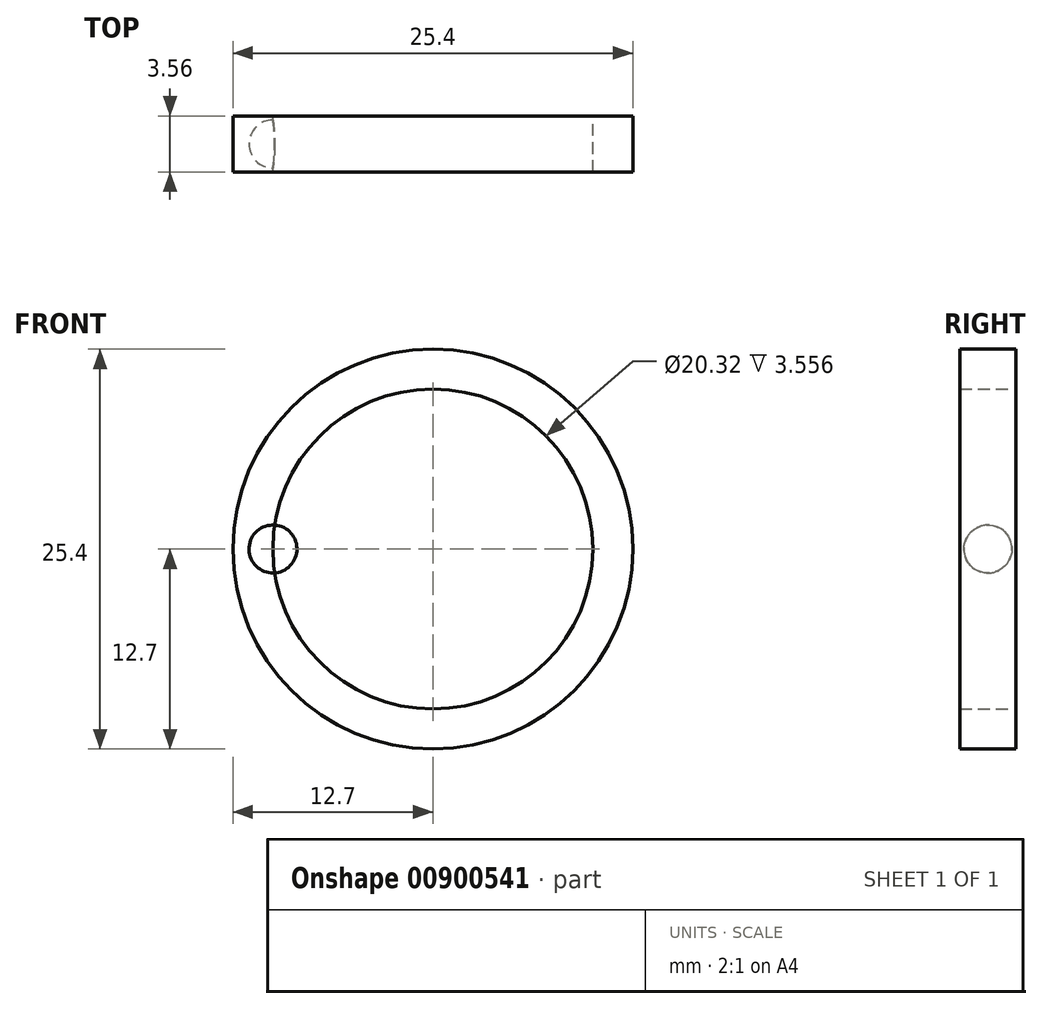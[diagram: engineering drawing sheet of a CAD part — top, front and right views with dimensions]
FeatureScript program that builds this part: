
annotation { "Feature Type Name" : "Feature", "Feature Type Description" : "" }
export const myFeature = defineFeature(function(context is Context, id is Id, definition is map)
    precondition{}
    {
        {
            var Q0;
            Q0=qCreatedBy(makeId("Front.planeOp"),FACE);
            var sketch = newSketch(context, id + "F0", { "sketchPlane" : qUnion([Q0])});
            skCircle(sketch, "E0", {"center": v(0, 0) * mm, "radius": 12.7 * mm});
            skCircle(sketch, "E1", {"center": v(0, 0) * mm, "radius": 10.16 * mm});
            skSolve(sketch);
        }
        {
            var Q0;
            Q0=makeQuery(id+"F0.imprint","IMPRINT",FACE,{"disambiguationData":[TD([[makeQuery(id+"F0.imprint","IMPRINT",EDGE,{"derivedFrom":sQuery(id+"F0.wireOp",EDGE,"E0")}),1.0]])]});
            extrude(context, id + "F1", {"entities" : qUnion([Q0]), "depth" : 1.78 * mm, "offsetDistance" : 25.4 * mm, "hasSecondDirection" : true, "secondDirectionOppositeDirection" : true, "secondDirectionDepth" : 1.78 * mm});
        }
        {
            var Q0;
            Q0=qCreatedBy(makeId("Front.planeOp"),FACE);
            var sketch = newSketch(context, id + "F2", { "sketchPlane" : qUnion([Q0])});
            skCircle(sketch, "E2.0.0", {"center": v(0, 0) * mm, "radius": 12.7 * mm});
            skLineSegment(sketch, "E3", {"start": v(-10.16, -1.52) * mm, "end": v(-10.16, 1.52) * mm});
            skArc(sketch, "E4", {"start": v(-10.16, -1.52) * mm, "mid": v(-8.64, 0) * mm, "end": v(-10.16, 1.52) * mm});
            skSolve(sketch);
        }
        {
            var Q0;
            Q0=makeQuery(id+"F2.imprint","IMPRINT",FACE,{"disambiguationData":[TD([[makeQuery(id+"F2.imprint","IMPRINT",EDGE,{"derivedFrom":sQuery(id+"F2.wireOp",EDGE,"E3")}),-1.0]])]});
            var Q1;
            Q1=sQuery(id+"F2.wireOp",EDGE,"E3");
            revolve(context, id + "F3", {"operationType" : NewBodyOperationType.REMOVE, "surfaceOperationType" : NewSurfaceOperationType.NEW, "entities" : qUnion([Q0]), "axis" : qUnion([Q1]), "revolveType" : RevolveType.FULL, "oppositeDirection" : true});
        }
    });
